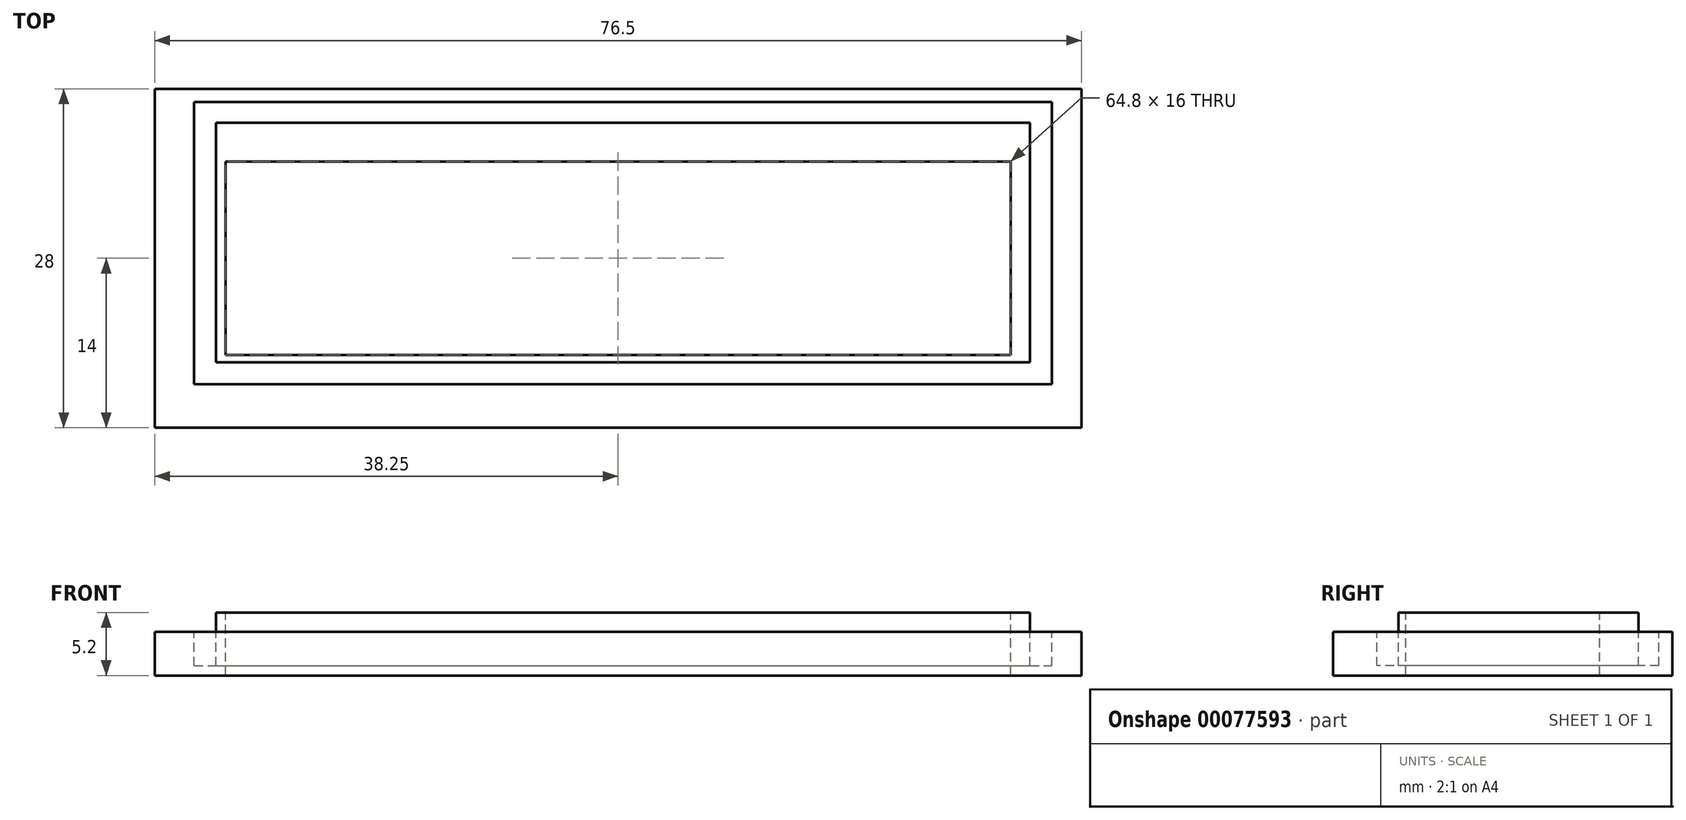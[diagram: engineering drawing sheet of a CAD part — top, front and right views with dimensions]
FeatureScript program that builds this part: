
annotation { "Feature Type Name" : "Feature", "Feature Type Description" : "" }
export const myFeature = defineFeature(function(context is Context, id is Id, definition is map)
    precondition{}
    {
        {
            var Q0;
            Q0=qCreatedBy(makeId("Top.planeOp"),FACE);
            var sketch = newSketch(context, id + "F0", { "sketchPlane" : qUnion([Q0])});
            skLineSegment(sketch, "E0.bottom", {"start": v(-38.25, 14) * mm, "end": v(38.25, 14) * mm});
            skLineSegment(sketch, "E0.top", {"start": v(-38.25, -14) * mm, "end": v(38.25, -14) * mm});
            skLineSegment(sketch, "E0.left", {"start": v(-38.25, 14) * mm, "end": v(-38.25, -14) * mm});
            skLineSegment(sketch, "E0.right", {"start": v(38.25, 14) * mm, "end": v(38.25, -14) * mm});
            skPoint(sketch, "E0.middle", {"position": v(0, 0) * mm});
            skSolve(sketch);
        }
        {
            var Q0;
            Q0=makeQuery(id+"F0.imprint","IMPRINT",FACE,{"disambiguationData":[TD([[makeQuery(id+"F0.imprint","IMPRINT",EDGE,{"derivedFrom":sQuery(id+"F0.wireOp",EDGE,"E0.bottom")}),-1.0]])]});
            extrude(context, id + "F1", {"entities" : qUnion([Q0]), "depth" : 3.6 * mm});
        }
        {
            var Q0;
            Q0=makeQuery(id+"F1.opExtrude","CAP_FACE",FACE,{"disambiguationData":[OSD([sQuery(id+"F0.wireOp",EDGE,"E0.bottom"),sQuery(id+"F0.wireOp",EDGE,"E0.top"),sQuery(id+"F0.wireOp",EDGE,"E0.left"),sQuery(id+"F0.wireOp",EDGE,"E0.right")])],"isStart":false});
            var sketch = newSketch(context, id + "F2", { "sketchPlane" : qUnion([Q0])});
            skLineSegment(sketch, "E1.bottom", {"start": v(-32.4, 8) * mm, "end": v(32.4, 8) * mm});
            skLineSegment(sketch, "E1.top", {"start": v(-32.4, -8) * mm, "end": v(32.4, -8) * mm});
            skLineSegment(sketch, "E1.left", {"start": v(-32.4, 8) * mm, "end": v(-32.4, -8) * mm});
            skLineSegment(sketch, "E1.right", {"start": v(32.4, 8) * mm, "end": v(32.4, -8) * mm});
            skLineSegment(sketch, "E2", {"start": v(0, -28.85) * mm, "end": v(0, 56.29) * mm, "construction": true});
            skLineSegment(sketch, "E3", {"start": v(-32.4, 8) * mm, "end": v(32.4, -8) * mm, "construction": true});
            skPoint(sketch, "E4", {"position": v(0, 0) * mm});
            skSolve(sketch);
        }
        {
            var Q0;
            Q0 = qSketchRegion(id + "F2", true);
            extrude(context, id + "F3", {"entities" : qUnion([Q0]), "operationType" : NewBodyOperationType.REMOVE, "oppositeDirection" : true, "depth" : 25 * mm});
        }
        {
            var Q0;
            Q0=makeQuery(id+"F1.opExtrude","CAP_FACE",FACE,{"disambiguationData":[OSD([sQuery(id+"F0.wireOp",EDGE,"E0.bottom"),sQuery(id+"F0.wireOp",EDGE,"E0.top"),sQuery(id+"F0.wireOp",EDGE,"E0.left"),sQuery(id+"F0.wireOp",EDGE,"E0.right")])],"isStart":false});
            var sketch = newSketch(context, id + "F4", { "sketchPlane" : qUnion([Q0])});
            skLineSegment(sketch, "E5.bottom", {"start": v(-35, 12.9) * mm, "end": v(35.8, 12.9) * mm});
            skLineSegment(sketch, "E5.top", {"start": v(-35, -10.4) * mm, "end": v(35.8, -10.4) * mm});
            skLineSegment(sketch, "E5.left", {"start": v(-35, 12.9) * mm, "end": v(-35, -10.4) * mm});
            skLineSegment(sketch, "E5.right", {"start": v(35.8, 12.9) * mm, "end": v(35.8, -10.4) * mm});
            skLineSegment(sketch, "E6.bottom", {"start": v(-33.2, 11.2) * mm, "end": v(34, 11.2) * mm});
            skLineSegment(sketch, "E6.top", {"start": v(-33.2, -8.6) * mm, "end": v(34, -8.6) * mm});
            skLineSegment(sketch, "E6.left", {"start": v(-33.2, 11.2) * mm, "end": v(-33.2, -8.6) * mm});
            skLineSegment(sketch, "E6.right", {"start": v(34, 11.2) * mm, "end": v(34, -8.6) * mm});
            skLineSegment(sketch, "E7", {"start": v(-33.2, 11.2) * mm, "end": v(34, -8.6) * mm, "construction": true});
            skPoint(sketch, "E8", {"position": v(0.4, 1.3) * mm});
            skLineSegment(sketch, "E9", {"start": v(0, 20.28) * mm, "end": v(0, -40.46) * mm, "construction": true});
            skLineSegment(sketch, "E10", {"start": v(-32.4, 8) * mm, "end": v(-32.4, -8) * mm, "construction": true});
            skLineSegment(sketch, "E11", {"start": v(-32.4, -8) * mm, "end": v(-32.4, 8) * mm, "construction": true});
            skPoint(sketch, "E12", {"position": v(-33.2, 1.3) * mm});
            skLineSegment(sketch, "E13", {"start": v(-32.4, 8) * mm, "end": v(32.4, -8) * mm, "construction": true});
            skPoint(sketch, "E14", {"position": v(0, 0) * mm});
            skSolve(sketch);
        }
        {
            var Q0;
            Q0 = qSketchRegion(id + "F4", true);
            extrude(context, id + "F5", {"entities" : qUnion([Q0]), "operationType" : NewBodyOperationType.REMOVE, "oppositeDirection" : true, "depth" : 2.8 * mm});
        }
        {
            var Q0;
            Q0=makeQuery(id+"F5.boolean.opBoolean","SPLIT",FACE,{"disambiguationData":[TD([makeQuery(id+"F3.boolean.opBoolean","COPY",FACE,{"derivedFrom":makeQuery(id+"F3.opExtrude","SWEPT_FACE",FACE,{"disambiguationData":[OSD([sQuery(id+"F2.wireOp",EDGE,"E1.bottom")])]})})])],"derivedFrom":makeQuery(id+"F1.opExtrude","CAP_FACE",FACE,{"disambiguationData":[OSD([sQuery(id+"F0.wireOp",EDGE,"E0.bottom"),sQuery(id+"F0.wireOp",EDGE,"E0.top"),sQuery(id+"F0.wireOp",EDGE,"E0.left"),sQuery(id+"F0.wireOp",EDGE,"E0.right")])],"isStart":false})});
            var sketch = newSketch(context, id + "F6", { "sketchPlane" : qUnion([Q0])});
            skLineSegment(sketch, "E15.bottom", {"start": v(-33.2, 11.2) * mm, "end": v(34, 11.2) * mm});
            skLineSegment(sketch, "E15.top", {"start": v(-33.2, -8.6) * mm, "end": v(34, -8.6) * mm});
            skLineSegment(sketch, "E15.left", {"start": v(-33.2, 11.2) * mm, "end": v(-33.2, -8.6) * mm});
            skLineSegment(sketch, "E15.right", {"start": v(34, 11.2) * mm, "end": v(34, -8.6) * mm});
            skLineSegment(sketch, "E16.bottom", {"start": v(-32.4, 8) * mm, "end": v(32.4, 8) * mm});
            skLineSegment(sketch, "E16.top", {"start": v(-32.4, -8) * mm, "end": v(32.4, -8) * mm});
            skLineSegment(sketch, "E16.left", {"start": v(-32.4, 8) * mm, "end": v(-32.4, -8) * mm});
            skLineSegment(sketch, "E16.right", {"start": v(32.4, 8) * mm, "end": v(32.4, -8) * mm});
            skSolve(sketch);
        }
        {
            var Q0;
            Q0 = qSketchRegion(id + "F6", true);
            extrude(context, id + "F7", {"entities" : qUnion([Q0]), "operationType" : NewBodyOperationType.ADD, "depth" : 1.6 * mm});
        }
    });
